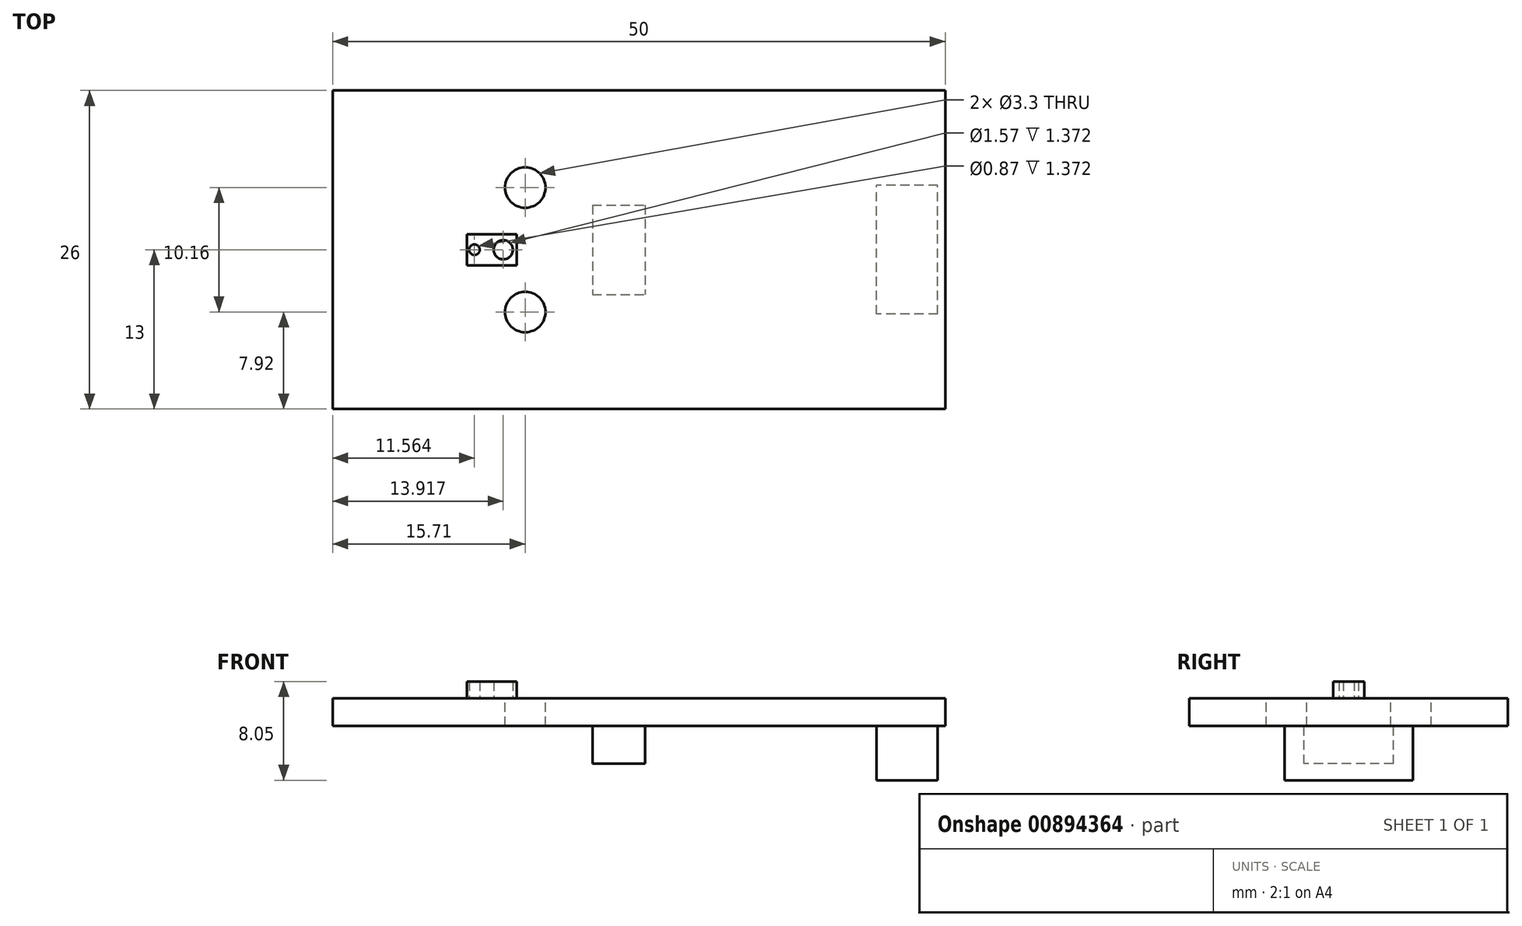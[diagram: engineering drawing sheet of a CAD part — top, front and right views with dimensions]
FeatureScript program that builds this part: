
annotation { "Feature Type Name" : "Feature", "Feature Type Description" : "" }
export const myFeature = defineFeature(function(context is Context, id is Id, definition is map)
    precondition{}
    {
        {
            var Q0;
            Q0=qCreatedBy(makeId("Top.planeOp"),FACE);
            var sketch = newSketch(context, id + "F0", { "sketchPlane" : qUnion([Q0])});
            skLineSegment(sketch, "E0.bottom", {"start": v(25, 13) * mm, "end": v(-25, 13) * mm});
            skLineSegment(sketch, "E0.top", {"start": v(25, -13) * mm, "end": v(-25, -13) * mm});
            skLineSegment(sketch, "E0.left", {"start": v(25, 13) * mm, "end": v(25, -13) * mm});
            skLineSegment(sketch, "E0.right", {"start": v(-25, 13) * mm, "end": v(-25, -13) * mm});
            skPoint(sketch, "E0.middle", {"position": v(0, 0) * mm});
            skSolve(sketch);
        }
        {
            var Q0;
            Q0=makeQuery(id+"F0.imprint","IMPRINT",FACE,{"disambiguationData":[TD([[makeQuery(id+"F0.imprint","IMPRINT",EDGE,{"derivedFrom":sQuery(id+"F0.wireOp",EDGE,"E0.bottom")}),1.0]])]});
            extrude(context, id + "F1", {"entities" : qUnion([Q0]), "depth" : 0.97 * mm, "offsetDistance" : 25.4 * mm});
        }
        {
            var Q0;
            Q0=makeQuery(id+"F1.opExtrude","SWEPT_BODY",BODY,{"disambiguationData":[OSD([sQuery(id+"F0.wireOp",EDGE,"E0.bottom"),sQuery(id+"F0.wireOp",EDGE,"E0.top"),sQuery(id+"F0.wireOp",EDGE,"E0.left"),sQuery(id+"F0.wireOp",EDGE,"E0.right")])]});
            transform(context, id + "F2", {"entities" : qUnion([Q0]), "transformType" : TransformType.TRANSLATION_3D, "dx" : 12 * mm, "dy" : 0 * mm, "dz" : 0 * mm, "makeCopy" : false});
        }
        {
            var Q0;
            Q0=makeQuery(id+"F1.opExtrude","CAP_FACE",FACE,{"disambiguationData":[OSD([sQuery(id+"F0.wireOp",EDGE,"E0.bottom"),sQuery(id+"F0.wireOp",EDGE,"E0.top"),sQuery(id+"F0.wireOp",EDGE,"E0.left"),sQuery(id+"F0.wireOp",EDGE,"E0.right")])],"isStart":true});
            var sketch = newSketch(context, id + "F3", { "sketchPlane" : qUnion([Q0])});
            skLineSegment(sketch, "E1.bottom", {"start": v(2.03, -1.27) * mm, "end": v(-2.03, -1.27) * mm});
            skLineSegment(sketch, "E1.top", {"start": v(2.03, 1.27) * mm, "end": v(-2.03, 1.27) * mm});
            skLineSegment(sketch, "E1.left", {"start": v(2.03, -1.27) * mm, "end": v(2.03, 1.27) * mm});
            skLineSegment(sketch, "E1.right", {"start": v(-2.03, -1.27) * mm, "end": v(-2.03, 1.27) * mm});
            skPoint(sketch, "E1.middle", {"position": v(0, 0) * mm});
            skCircle(sketch, "E2", {"center": v(0.92, 0) * mm, "radius": 0.78 * mm});
            skCircle(sketch, "E3", {"center": v(-1.44, 0) * mm, "radius": 0.43 * mm});
            skSolve(sketch);
        }
        {
            var Q0;
            Q0 = qSketchRegion(id + "F3", true);
            extrude(context, id + "F4", {"entities" : qUnion([Q0]), "operationType" : NewBodyOperationType.ADD, "oppositeDirection" : true, "depth" : 2.34 * mm, "offsetDistance" : 25.4 * mm});
        }
        {
            var Q0;
            Q0=makeQuery(id+"F4.boolean.opBoolean","SPLIT",FACE,{"disambiguationData":[TD([makeQuery(id+"F4.opExtrude","SWEPT_FACE",FACE,{"disambiguationData":[OSD([sQuery(id+"F3.wireOp",EDGE,"E2")])]})])],"derivedFrom":makeQuery(id+"F1.opExtrude","CAP_FACE",FACE,{"disambiguationData":[OSD([sQuery(id+"F0.wireOp",EDGE,"E0.bottom"),sQuery(id+"F0.wireOp",EDGE,"E0.top"),sQuery(id+"F0.wireOp",EDGE,"E0.left"),sQuery(id+"F0.wireOp",EDGE,"E0.right")])],"isStart":true})});
            var Q1;
            Q1=makeQuery(id+"F4.boolean.opBoolean","SPLIT",FACE,{"disambiguationData":[TD([makeQuery(id+"F4.opExtrude","SWEPT_FACE",FACE,{"disambiguationData":[OSD([sQuery(id+"F3.wireOp",EDGE,"E3")])]})])],"derivedFrom":makeQuery(id+"F1.opExtrude","CAP_FACE",FACE,{"disambiguationData":[OSD([sQuery(id+"F0.wireOp",EDGE,"E0.bottom"),sQuery(id+"F0.wireOp",EDGE,"E0.top"),sQuery(id+"F0.wireOp",EDGE,"E0.left"),sQuery(id+"F0.wireOp",EDGE,"E0.right")])],"isStart":true})});
            extrude(context, id + "F5", {"entities" : qUnion([Q0, Q1]), "operationType" : NewBodyOperationType.ADD, "depth" : 1.27 * mm, "offsetDistance" : 25.4 * mm});
        }
        {
            var Q0;
            Q0=makeQuery(id+"F5.opExtrude","CAP_FACE",FACE,{"disambiguationData":[OSD([sQuery(id+"F0.wireOp",EDGE,"E0.bottom"),sQuery(id+"F0.wireOp",EDGE,"E0.top"),sQuery(id+"F0.wireOp",EDGE,"E0.left"),sQuery(id+"F0.wireOp",EDGE,"E0.right")])],"isStart":false});
            var sketch = newSketch(context, id + "F6", { "sketchPlane" : qUnion([Q0])});
            skLineSegment(sketch, "E4.bottom", {"start": v(-2.15, -3.64) * mm, "end": v(2.15, -3.64) * mm});
            skLineSegment(sketch, "E4.top", {"start": v(-2.15, 3.64) * mm, "end": v(2.15, 3.64) * mm});
            skLineSegment(sketch, "E4.left", {"start": v(-2.15, -3.64) * mm, "end": v(-2.15, 3.64) * mm});
            skLineSegment(sketch, "E4.right", {"start": v(2.15, -3.64) * mm, "end": v(2.15, 3.64) * mm});
            skPoint(sketch, "E4.middle", {"position": v(0, 0) * mm});
            skSolve(sketch);
        }
        {
            var Q0;
            {var subQ0=sQuery(id+"F0.wireOp",EDGE,"E0.left");var subQ1=sQuery(id+"F0.wireOp",EDGE,"E0.top");var subQ2=sQuery(id+"F0.wireOp",EDGE,"E0.right");var subQ3=sQuery(id+"F0.wireOp",EDGE,"E0.bottom");Q0=makeQuery(id+"F4.boolean.opBoolean","SPLIT",FACE,{"disambiguationData":[TD([makeQuery(id+"F1.opExtrude","SWEPT_FACE",FACE,{"disambiguationData":[OSD([subQ3])]})])],"derivedFrom":makeQuery(id+"F1.opExtrude","CAP_FACE",FACE,{"disambiguationData":[OSD([subQ3,subQ1,subQ0,subQ2])],"isStart":false})});}
            var sketch = newSketch(context, id + "F7", { "sketchPlane" : qUnion([Q0])});
            skCircle(sketch, "E5", {"center": v(2.7, 5.08) * mm, "radius": 1.65 * mm});
            skCircle(sketch, "E6", {"center": v(2.7, -5.08) * mm, "radius": 1.65 * mm});
            skSolve(sketch);
        }
        {
            var Q0;
            Q0=makeQuery(id+"F7.imprint","IMPRINT",FACE,{"disambiguationData":[TD([[makeQuery(id+"F7.imprint","IMPRINT",EDGE,{"derivedFrom":sQuery(id+"F7.wireOp",EDGE,"E5")}),1.0]])]});
            var Q1;
            Q1=makeQuery(id+"F7.imprint","IMPRINT",FACE,{"disambiguationData":[TD([[makeQuery(id+"F7.imprint","IMPRINT",EDGE,{"derivedFrom":sQuery(id+"F7.wireOp",EDGE,"E6")}),1.0]])]});
            var Q2;
            Q2=sQuery(id+"F7.wireOp",EDGE,"E5");
            var Q3;
            Q3=sQuery(id+"F7.wireOp",EDGE,"E6");
            extrude(context, id + "F8", {"entities" : qUnion([Q0, Q1]), "operationType" : NewBodyOperationType.REMOVE, "surfaceEntities" : qUnion([Q2, Q3]), "oppositeDirection" : true, "depth" : 25.4 * mm, "offsetDistance" : 25.4 * mm});
        }
        {
            var Q0;
            Q0=makeQuery(id+"F6.imprint","IMPRINT",FACE,{"disambiguationData":[TD([[makeQuery(id+"F6.imprint","IMPRINT",EDGE,{"derivedFrom":sQuery(id+"F6.wireOp",EDGE,"E4.bottom")}),1.0]])]});
            extrude(context, id + "F9", {"entities" : qUnion([Q0]), "depth" : 3.1 * mm, "offsetDistance" : 25.4 * mm});
        }
        {
            var Q0;
            Q0=makeQuery(id+"F9.opExtrude","SWEPT_BODY",BODY,{"disambiguationData":[OSD([sQuery(id+"F6.wireOp",EDGE,"E4.bottom"),sQuery(id+"F6.wireOp",EDGE,"E4.top"),sQuery(id+"F6.wireOp",EDGE,"E4.left"),sQuery(id+"F6.wireOp",EDGE,"E4.right")])]});
            transform(context, id + "F10", {"entities" : qUnion([Q0]), "transformType" : TransformType.TRANSLATION_3D, "dx" : 10.35 * mm, "dy" : 0 * mm, "dz" : 0 * mm, "makeCopy" : false});
        }
        {
            var Q0;
            Q0=makeQuery(id+"F5.opExtrude","CAP_FACE",FACE,{"disambiguationData":[OSD([sQuery(id+"F0.wireOp",EDGE,"E0.bottom"),sQuery(id+"F0.wireOp",EDGE,"E0.top"),sQuery(id+"F0.wireOp",EDGE,"E0.left"),sQuery(id+"F0.wireOp",EDGE,"E0.right")])],"isStart":false});
            var sketch = newSketch(context, id + "F11", { "sketchPlane" : qUnion([Q0])});
            skLineSegment(sketch, "E7.bottom", {"start": v(23.65, 5.25) * mm, "end": v(18.65, 5.25) * mm});
            skLineSegment(sketch, "E7.top", {"start": v(23.65, -5.25) * mm, "end": v(18.65, -5.25) * mm});
            skLineSegment(sketch, "E7.left", {"start": v(23.65, 5.25) * mm, "end": v(23.65, -5.25) * mm});
            skLineSegment(sketch, "E7.right", {"start": v(18.65, 5.25) * mm, "end": v(18.65, -5.25) * mm});
            skPoint(sketch, "E7.middle", {"position": v(21.15, 0) * mm});
            skSolve(sketch);
        }
        {
            var Q0;
            Q0=makeQuery(id+"F11.imprint","IMPRINT",FACE,{"disambiguationData":[TD([[makeQuery(id+"F11.imprint","IMPRINT",EDGE,{"derivedFrom":sQuery(id+"F11.wireOp",EDGE,"E7.bottom")}),1.0]])]});
            extrude(context, id + "F12", {"entities" : qUnion([Q0]), "depth" : 4.44 * mm, "offsetDistance" : 25.4 * mm});
        }
        {
            var Q0;
            Q0=makeQuery(id+"F12.opExtrude","SWEPT_BODY",BODY,{"disambiguationData":[OSD([sQuery(id+"F11.wireOp",EDGE,"E7.bottom"),sQuery(id+"F11.wireOp",EDGE,"E7.top"),sQuery(id+"F11.wireOp",EDGE,"E7.left"),sQuery(id+"F11.wireOp",EDGE,"E7.right")])]});
            transform(context, id + "F13", {"entities" : qUnion([Q0]), "transformType" : TransformType.TRANSLATION_3D, "dx" : 8.64 * mm, "dy" : 0 * mm, "dz" : 0 * mm, "makeCopy" : false});
        }
        {
            var Q0;
            Q0=makeQuery(id+"F12.opExtrude","SWEPT_BODY",BODY,{"disambiguationData":[OSD([sQuery(id+"F11.wireOp",EDGE,"E7.bottom"),sQuery(id+"F11.wireOp",EDGE,"E7.top"),sQuery(id+"F11.wireOp",EDGE,"E7.left"),sQuery(id+"F11.wireOp",EDGE,"E7.right")])]});
            transform(context, id + "F14", {"entities" : qUnion([Q0]), "transformType" : TransformType.TRANSLATION_3D, "dx" : 4.1 * mm, "dy" : 0 * mm, "dz" : 0 * mm, "makeCopy" : false});
        }
    });
